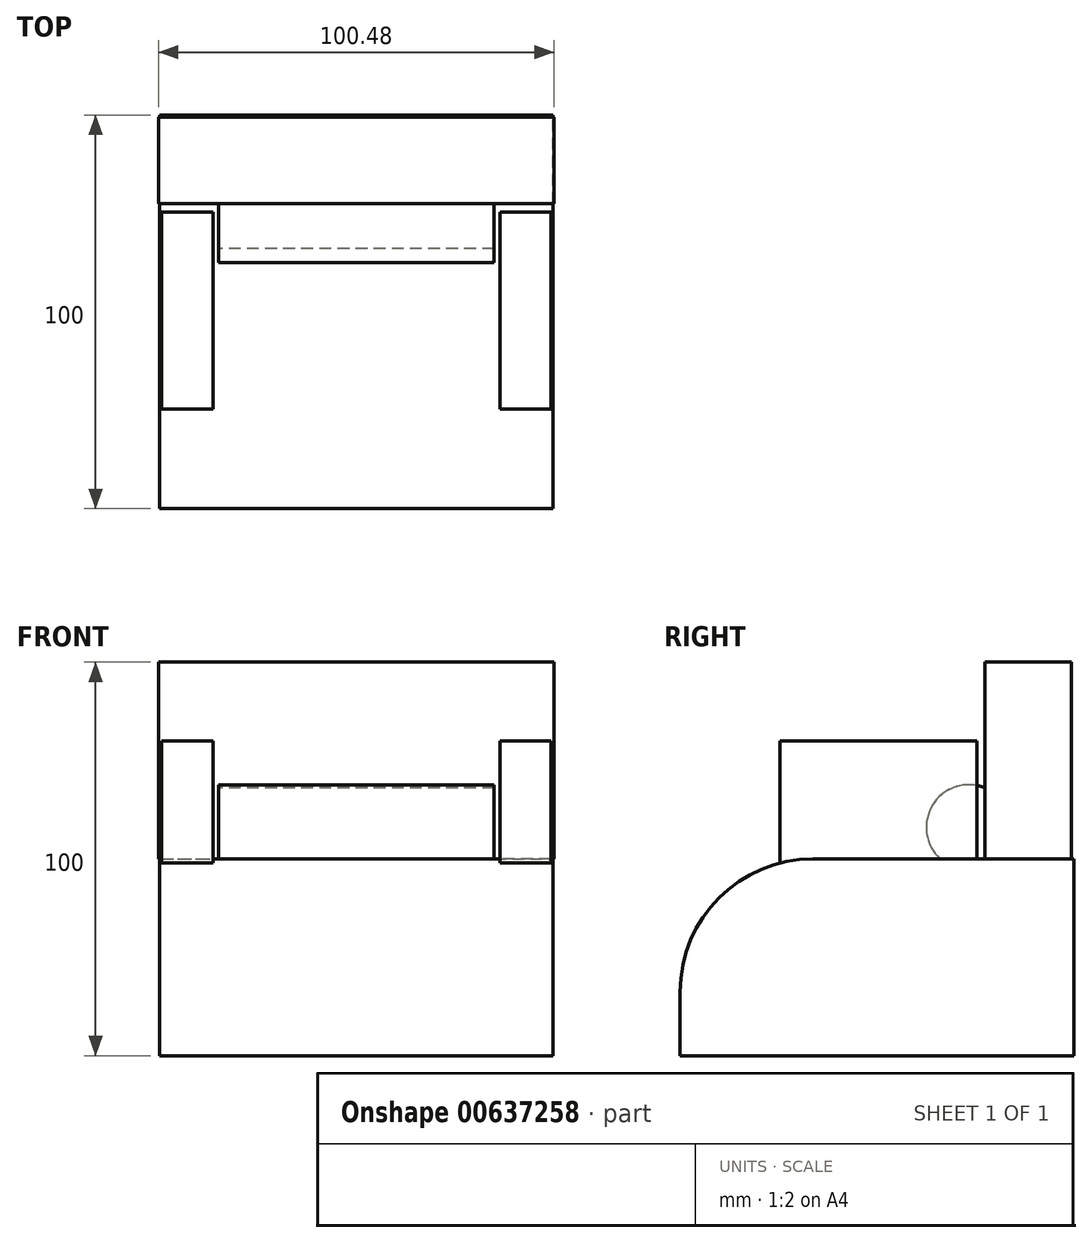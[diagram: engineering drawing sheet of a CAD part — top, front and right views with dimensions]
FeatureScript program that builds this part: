
annotation { "Feature Type Name" : "Feature", "Feature Type Description" : "" }
export const myFeature = defineFeature(function(context is Context, id is Id, definition is map)
    precondition{}
    {
        {
            var Q0;
            Q0=qCreatedBy(makeId("Top.planeOp"),FACE);
            var sketch = newSketch(context, id + "F0", { "sketchPlane" : qUnion([Q0])});
            skLineSegment(sketch, "E0.bottom", {"start": v(50, -50) * mm, "end": v(-50, -50) * mm});
            skLineSegment(sketch, "E0.top", {"start": v(50, 50) * mm, "end": v(-50, 50) * mm});
            skLineSegment(sketch, "E0.left", {"start": v(50, -50) * mm, "end": v(50, 50) * mm});
            skLineSegment(sketch, "E0.right", {"start": v(-50, -50) * mm, "end": v(-50, 50) * mm});
            skPoint(sketch, "E0.middle", {"position": v(0, 0) * mm});
            skSolve(sketch);
        }
        {
            var Q0;
            Q0=makeQuery(id+"F0.imprint","IMPRINT",FACE,{"disambiguationData":[TD([[makeQuery(id+"F0.imprint","IMPRINT",EDGE,{"derivedFrom":sQuery(id+"F0.wireOp",EDGE,"E0.bottom")}),-1.0]])]});
            extrude(context, id + "F1", {"entities" : qUnion([Q0]), "depth" : 50 * mm, "offsetDistance" : 25 * mm});
        }
        {
            var Q0;
            Q0=qCreatedBy(makeId("Top.planeOp"),FACE);
            cPlane(context, id + "F2", {"entities" : qUnion([Q0]), "cplaneType" : CPlaneType.OFFSET, "offset" : 50 * mm, "width" : 150 * mm, "height" : 150 * mm});
        }
        {
            var Q0;
            Q0=qCreatedBy(id+"F2.planeOp",FACE);
            var sketch = newSketch(context, id + "F3", { "sketchPlane" : qUnion([Q0])});
            skLineSegment(sketch, "E1.bottom", {"start": v(-50.24, 49.44) * mm, "end": v(49.76, 49.44) * mm});
            skLineSegment(sketch, "E1.top", {"start": v(-50.24, 27.44) * mm, "end": v(49.76, 27.44) * mm});
            skLineSegment(sketch, "E1.left", {"start": v(-50.24, 49.44) * mm, "end": v(-50.24, 27.44) * mm});
            skLineSegment(sketch, "E1.right", {"start": v(49.76, 49.44) * mm, "end": v(49.76, 27.44) * mm});
            skLineSegment(sketch, "E2.bottom", {"start": v(-50.24, 27.44) * mm, "end": v(-42.63, 27.44) * mm});
            skLineSegment(sketch, "E2.top", {"start": v(-50.24, -50.07) * mm, "end": v(-42.63, -50.07) * mm});
            skLineSegment(sketch, "E2.left", {"start": v(-50.24, 27.44) * mm, "end": v(-50.24, -50.07) * mm});
            skLineSegment(sketch, "E2.right", {"start": v(-42.63, 27.44) * mm, "end": v(-42.63, -50.07) * mm});
            skSolve(sketch);
        }
        {
            var Q0;
            Q0=makeQuery(id+"F3.imprint","IMPRINT",FACE,{"disambiguationData":[TD([[makeQuery(id+"F3.imprint","IMPRINT",EDGE,{"derivedFrom":sQuery(id+"F3.wireOp",EDGE,"E1.bottom")}),-1.0]])]});
            extrude(context, id + "F4", {"entities" : qUnion([Q0]), "operationType" : NewBodyOperationType.ADD, "depth" : 50 * mm, "offsetDistance" : 25 * mm});
        }
        {
            var Q0;
            Q0=qCreatedBy(id+"F2.planeOp",FACE);
            var sketch = newSketch(context, id + "F5", { "sketchPlane" : qUnion([Q0])});
            skLineSegment(sketch, "E3.bottom", {"start": v(-49.43, 25.35) * mm, "end": v(-36.43, 25.35) * mm});
            skLineSegment(sketch, "E3.top", {"start": v(-49.43, -24.65) * mm, "end": v(-36.43, -24.65) * mm});
            skLineSegment(sketch, "E3.left", {"start": v(-49.43, 25.35) * mm, "end": v(-49.43, -24.65) * mm});
            skLineSegment(sketch, "E3.right", {"start": v(-36.43, 25.35) * mm, "end": v(-36.43, -24.65) * mm});
            skSolve(sketch);
        }
        {
            var Q0;
            Q0 = qSketchRegion(id + "F5", true);
            extrude(context, id + "F6", {"entities" : qUnion([Q0]), "operationType" : NewBodyOperationType.ADD, "depth" : 30 * mm, "offsetDistance" : 25 * mm});
        }
        {
            var Q0;
            Q0=makeQuery(id+"F1.opExtrude","SWEPT_BODY",BODY,{"disambiguationData":[OSD([sQuery(id+"F0.wireOp",EDGE,"E0.bottom"),sQuery(id+"F0.wireOp",EDGE,"E0.top"),sQuery(id+"F0.wireOp",EDGE,"E0.left"),sQuery(id+"F0.wireOp",EDGE,"E0.right")])]});
            var Q1;
            Q1=qCreatedBy(makeId("Right.planeOp"),FACE);
            mirror(context, id + "F7", {"operationType" : NewBodyOperationType.ADD, "entities" : qUnion([Q0]), "mirrorPlane" : qUnion([Q1])});
        }
        {
            var Q0;
            Q0=qCreatedBy(makeId("Right.planeOp"),FACE);
            var sketch = newSketch(context, id + "F8", { "sketchPlane" : qUnion([Q0])});
            skCircle(sketch, "E4", {"center": v(23.4, 58) * mm, "radius": 10.85 * mm});
            skSolve(sketch);
        }
        {
            var Q0;
            Q0 = qSketchRegion(id + "F8", true);
            extrude(context, id + "F9", {"entities" : qUnion([Q0]), "operationType" : NewBodyOperationType.ADD, "endBound" : BoundingType.SYMMETRIC, "depth" : 70 * mm, "offsetDistance" : 25 * mm});
        }
        {
            var Q0;
            Q0=makeQuery(id+"F1.opExtrude","CAP_EDGE",EDGE,{"disambiguationData":[OSD([sQuery(id+"F0.wireOp",EDGE,"E0.bottom")])],"isStart":false});
            fillet(context, id + "F10", {"entities" : qUnion([Q0]), "radius" : 33.8 * mm, "tangentPropagation" : true, "allowEdgeOverflow" : false});
        }
    });
